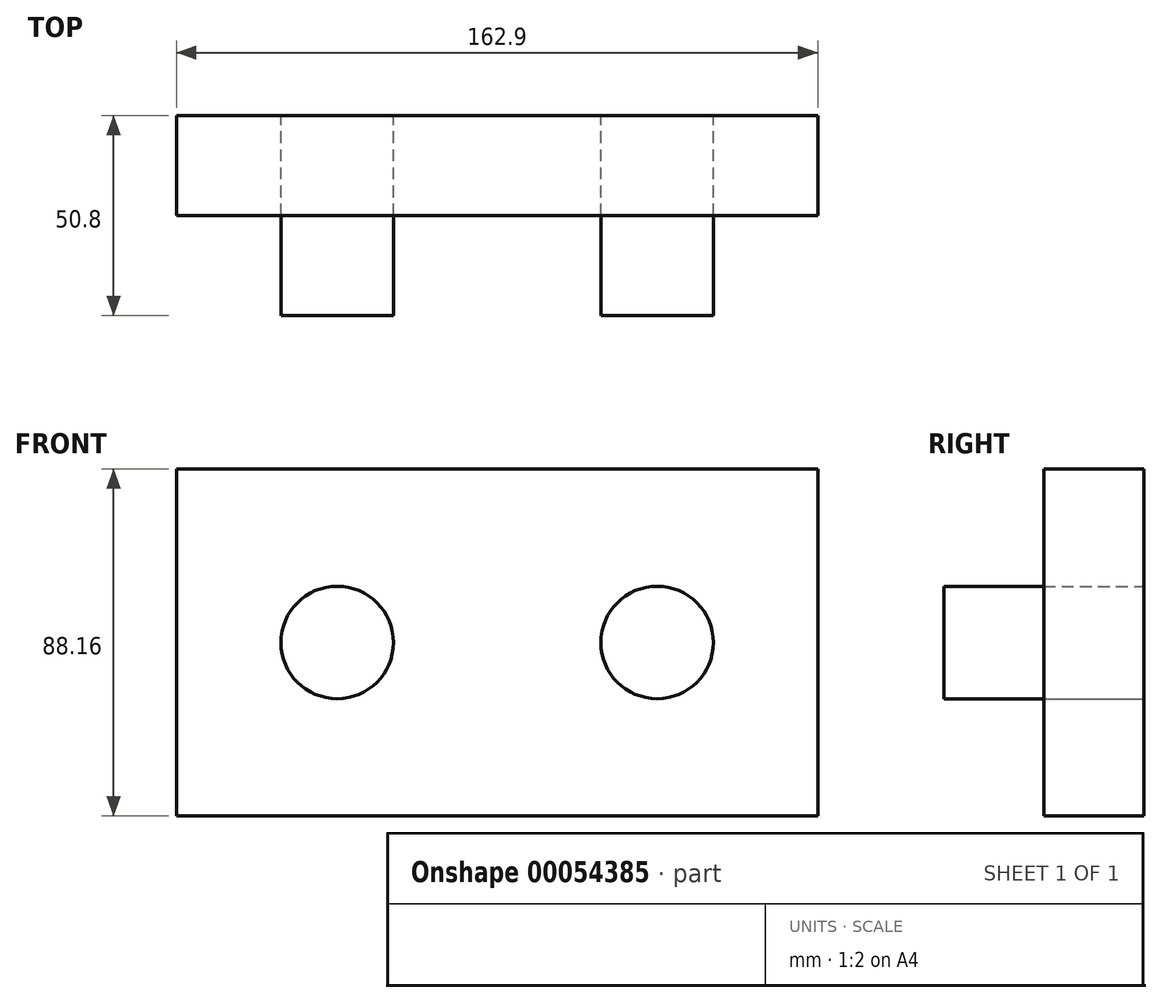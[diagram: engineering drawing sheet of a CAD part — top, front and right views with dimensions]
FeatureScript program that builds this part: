
annotation { "Feature Type Name" : "Feature", "Feature Type Description" : "" }
export const myFeature = defineFeature(function(context is Context, id is Id, definition is map)
    precondition{}
    {
        {
            var Q0;
            Q0=qCreatedBy(makeId("Front.planeOp"),FACE);
            var sketch = newSketch(context, id + "F0", { "sketchPlane" : qUnion([Q0])});
            skLineSegment(sketch, "E0.rect.bottom", {"start": v(81.45, 44.08) * mm, "end": v(-81.45, 44.08) * mm});
            skLineSegment(sketch, "E0.rect.top", {"start": v(81.45, -44.08) * mm, "end": v(-81.45, -44.08) * mm});
            skLineSegment(sketch, "E0.rect.left", {"start": v(81.45, 44.08) * mm, "end": v(81.45, -44.08) * mm});
            skLineSegment(sketch, "E0.rect.right", {"start": v(-81.45, 44.08) * mm, "end": v(-81.45, -44.08) * mm});
            skPoint(sketch, "E0.rect.middle", {"position": v(0, 0) * mm});
            skLineSegment(sketch, "E1", {"start": v(0, -44.08) * mm, "end": v(0, 44.08) * mm, "construction": true});
            skLineSegment(sketch, "E2", {"start": v(-40.64, 44.08) * mm, "end": v(-40.64, -44.08) * mm, "construction": true});
            skLineSegment(sketch, "E3", {"start": v(40.64, 44.08) * mm, "end": v(40.64, -44.08) * mm, "construction": true});
            skCircle(sketch, "E4", {"center": v(-40.64, 0) * mm, "radius": 14.29 * mm});
            skCircle(sketch, "E5", {"center": v(40.64, 0) * mm, "radius": 14.29 * mm});
            skSolve(sketch);
        }
        {
            var Q0;
            Q0=makeQuery(id+"F0.imprint","IMPRINT",FACE,{"disambiguationData":[TD([[makeQuery(id+"F0.imprint","IMPRINT",EDGE,{"derivedFrom":sQuery(id+"F0.wireOp",EDGE,"E4")}),1.0]])]});
            var Q1;
            Q1=makeQuery(id+"F0.imprint","IMPRINT",FACE,{"disambiguationData":[TD([[makeQuery(id+"F0.imprint","IMPRINT",EDGE,{"derivedFrom":sQuery(id+"F0.wireOp",EDGE,"E5")}),1.0]])]});
            var Q2;
            Q2=makeQuery(id+"F0.imprint","IMPRINT",FACE,{"disambiguationData":[TD([[makeQuery(id+"F0.imprint","IMPRINT",EDGE,{"derivedFrom":sQuery(id+"F0.wireOp",EDGE,"E0.rect.bottom")}),1.0]])]});
            extrude(context, id + "F1", {"entities" : qUnion([Q0, Q1, Q2]), "depth" : 25.4 * mm});
        }
        {
            var Q0;
            Q0=makeQuery(id+"F0.imprint","IMPRINT",FACE,{"disambiguationData":[TD([[makeQuery(id+"F0.imprint","IMPRINT",EDGE,{"derivedFrom":sQuery(id+"F0.wireOp",EDGE,"E4")}),1.0]])]});
            var Q1;
            Q1=makeQuery(id+"F0.imprint","IMPRINT",FACE,{"disambiguationData":[TD([[makeQuery(id+"F0.imprint","IMPRINT",EDGE,{"derivedFrom":sQuery(id+"F0.wireOp",EDGE,"E5")}),1.0]])]});
            extrude(context, id + "F2", {"entities" : qUnion([Q0, Q1]), "depth" : 50.8 * mm});
        }
    });
